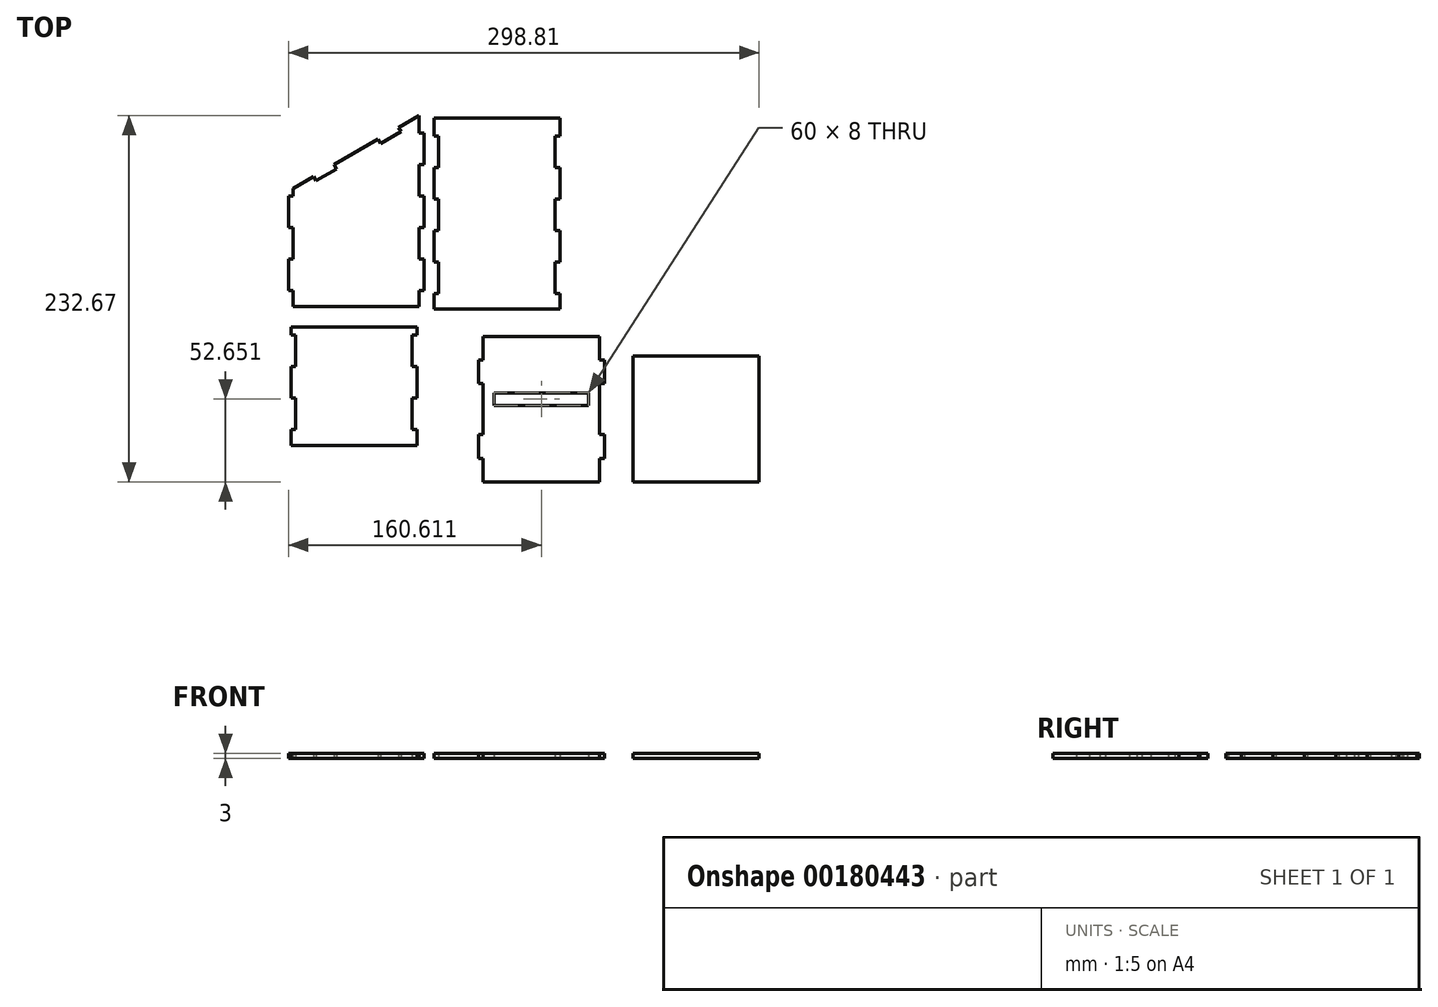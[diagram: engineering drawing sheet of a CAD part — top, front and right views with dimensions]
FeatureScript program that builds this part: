
annotation { "Feature Type Name" : "Feature", "Feature Type Description" : "" }
export const myFeature = defineFeature(function(context is Context, id is Id, definition is map)
    precondition{}
    {
        {
            var Q0;
            Q0=qCreatedBy(makeId("Top.planeOp"),FACE);
            var sketch = newSketch(context, id + "F0", { "sketchPlane" : qUnion([Q0])});
            skLineSegment(sketch, "E0.bottom", {"start": v(175, 135) * mm, "end": v(-175, 135) * mm, "construction": true});
            skLineSegment(sketch, "E0.top", {"start": v(175, -135) * mm, "end": v(-175, -135) * mm, "construction": true});
            skLineSegment(sketch, "E0.left", {"start": v(175, 135) * mm, "end": v(175, -135) * mm, "construction": true});
            skLineSegment(sketch, "E0.right", {"start": v(-175, 135) * mm, "end": v(-175, -135) * mm, "construction": true});
            skPoint(sketch, "E0.middle", {"position": v(0, 0) * mm});
            skLineSegment(sketch, "E1.bottom", {"start": v(-144.86, 75.27) * mm, "end": v(-131.87, 82.77) * mm});
            skLineSegment(sketch, "E1.top", {"start": v(-144.86, 0.27) * mm, "end": v(-64.86, 0.27) * mm});
            skLineSegment(sketch, "E1.left", {"start": v(-144.86, 75.27) * mm, "end": v(-144.86, 70.27) * mm});
            skLineSegment(sketch, "E1.right", {"start": v(-64.86, 121.46) * mm, "end": v(-64.86, 110.27) * mm});
            skLineSegment(sketch, "E2.bottom", {"start": v(-55.51, 119.78) * mm, "end": v(24.49, 119.78) * mm});
            skLineSegment(sketch, "E2.top", {"start": v(-55.51, -1.41) * mm, "end": v(24.49, -1.41) * mm});
            skLineSegment(sketch, "E2.left", {"start": v(-55.51, 119.78) * mm, "end": v(-55.51, 108.59) * mm});
            skLineSegment(sketch, "E2.right", {"start": v(24.49, 119.78) * mm, "end": v(24.49, 108.59) * mm});
            skLineSegment(sketch, "E3.bottom", {"start": v(52.66, 73.13) * mm, "end": v(132.66, 119.32) * mm});
            skLineSegment(sketch, "E3.top", {"start": v(52.66, -1.87) * mm, "end": v(132.66, -1.87) * mm});
            skLineSegment(sketch, "E3.left", {"start": v(52.66, 73.13) * mm, "end": v(52.66, -1.87) * mm});
            skLineSegment(sketch, "E3.right", {"start": v(132.66, 119.32) * mm, "end": v(132.66, -1.87) * mm});
            skLineSegment(sketch, "E4.bottom", {"start": v(-146.25, -12.92) * mm, "end": v(-66.25, -12.92) * mm});
            skLineSegment(sketch, "E4.top", {"start": v(-146.25, -87.92) * mm, "end": v(-66.25, -87.92) * mm});
            skLineSegment(sketch, "E4.left", {"start": v(-146.25, -12.92) * mm, "end": v(-146.25, -17.92) * mm});
            skLineSegment(sketch, "E4.right", {"start": v(-66.25, -12.92) * mm, "end": v(-66.25, -17.92) * mm});
            skLineSegment(sketch, "E5.bottom", {"start": v(-24.25, -18.83) * mm, "end": v(49.75, -18.83) * mm});
            skLineSegment(sketch, "E5.top", {"start": v(-24.25, -111.21) * mm, "end": v(49.75, -111.21) * mm});
            skLineSegment(sketch, "E5.left", {"start": v(-24.25, -18.83) * mm, "end": v(-24.25, -33.83) * mm});
            skLineSegment(sketch, "E5.right", {"start": v(49.75, -18.83) * mm, "end": v(49.75, -33.83) * mm});
            skLineSegment(sketch, "E6.bottom", {"start": v(-17.25, -54.56) * mm, "end": v(42.75, -54.56) * mm});
            skLineSegment(sketch, "E6.top", {"start": v(-17.25, -62.56) * mm, "end": v(42.75, -62.56) * mm});
            skLineSegment(sketch, "E6.left", {"start": v(-17.25, -54.56) * mm, "end": v(-17.25, -62.56) * mm});
            skLineSegment(sketch, "E6.right", {"start": v(42.75, -54.56) * mm, "end": v(42.75, -62.56) * mm});
            skLineSegment(sketch, "E7", {"start": v(12.75, -18.83) * mm, "end": v(12.75, -54.56) * mm, "construction": true});
            skLineSegment(sketch, "E8", {"start": v(-64.86, 70.27) * mm, "end": v(-61.86, 70.27) * mm});
            skLineSegment(sketch, "E9", {"start": v(-61.86, 70.27) * mm, "end": v(-61.86, 50.27) * mm});
            skLineSegment(sketch, "E10", {"start": v(-61.86, 50.27) * mm, "end": v(-64.86, 50.27) * mm});
            skLineSegment(sketch, "E11", {"start": v(-55.51, 68.59) * mm, "end": v(-52.51, 68.59) * mm});
            skLineSegment(sketch, "E12", {"start": v(-52.51, 68.59) * mm, "end": v(-52.51, 48.59) * mm});
            skLineSegment(sketch, "E13", {"start": v(-52.51, 48.59) * mm, "end": v(-55.51, 48.59) * mm});
            skLineSegment(sketch, "E14", {"start": v(-64.86, 30.27) * mm, "end": v(-61.86, 30.27) * mm});
            skLineSegment(sketch, "E15", {"start": v(-61.86, 30.27) * mm, "end": v(-61.86, 10.27) * mm});
            skLineSegment(sketch, "E16", {"start": v(-61.86, 10.27) * mm, "end": v(-64.86, 10.27) * mm});
            skLineSegment(sketch, "E17", {"start": v(-55.51, 28.59) * mm, "end": v(-52.51, 28.59) * mm});
            skLineSegment(sketch, "E18", {"start": v(-52.51, 28.59) * mm, "end": v(-52.51, 8.59) * mm});
            skLineSegment(sketch, "E19", {"start": v(-52.51, 8.59) * mm, "end": v(-55.51, 8.59) * mm});
            skLineSegment(sketch, "E20.trimOffspring", {"start": v(-64.86, 50.27) * mm, "end": v(-64.86, 30.27) * mm});
            skLineSegment(sketch, "E21.trimOffspring", {"start": v(-64.86, 10.27) * mm, "end": v(-64.86, 0.27) * mm});
            skLineSegment(sketch, "E22.trimOffspring", {"start": v(-55.51, 8.59) * mm, "end": v(-55.51, -1.41) * mm});
            skLineSegment(sketch, "E23.trimOffspring", {"start": v(-55.51, 48.59) * mm, "end": v(-55.51, 28.59) * mm});
            skLineSegment(sketch, "E24", {"start": v(-64.86, 90.27) * mm, "end": v(-61.86, 90.27) * mm});
            skLineSegment(sketch, "E25", {"start": v(-61.86, 90.27) * mm, "end": v(-61.86, 110.27) * mm});
            skLineSegment(sketch, "E26", {"start": v(-61.86, 110.27) * mm, "end": v(-64.86, 110.27) * mm});
            skLineSegment(sketch, "E27.trimOffspring", {"start": v(-64.86, 90.27) * mm, "end": v(-64.86, 70.27) * mm});
            skLineSegment(sketch, "E28", {"start": v(-55.51, 88.59) * mm, "end": v(-52.51, 88.59) * mm});
            skLineSegment(sketch, "E29", {"start": v(-52.51, 88.59) * mm, "end": v(-52.51, 108.59) * mm});
            skLineSegment(sketch, "E30", {"start": v(-52.51, 108.59) * mm, "end": v(-55.51, 108.59) * mm});
            skLineSegment(sketch, "E31.trimOffspring", {"start": v(-55.51, 88.59) * mm, "end": v(-55.51, 68.59) * mm});
            skLineSegment(sketch, "E32", {"start": v(24.49, 108.59) * mm, "end": v(21.49, 108.59) * mm});
            skLineSegment(sketch, "E33", {"start": v(21.49, 108.59) * mm, "end": v(21.49, 88.59) * mm});
            skLineSegment(sketch, "E34", {"start": v(21.49, 88.59) * mm, "end": v(24.49, 88.59) * mm});
            skLineSegment(sketch, "E35", {"start": v(24.49, 68.59) * mm, "end": v(21.49, 68.59) * mm});
            skLineSegment(sketch, "E36", {"start": v(21.49, 68.59) * mm, "end": v(21.49, 48.59) * mm});
            skLineSegment(sketch, "E37", {"start": v(21.49, 48.59) * mm, "end": v(24.49, 48.59) * mm});
            skLineSegment(sketch, "E38", {"start": v(24.49, 28.59) * mm, "end": v(21.49, 28.59) * mm});
            skLineSegment(sketch, "E39", {"start": v(21.49, 28.59) * mm, "end": v(21.49, 8.59) * mm});
            skLineSegment(sketch, "E40", {"start": v(21.49, 8.59) * mm, "end": v(24.49, 8.59) * mm});
            skLineSegment(sketch, "E41.trimOffspring", {"start": v(24.49, 88.59) * mm, "end": v(24.49, 68.59) * mm});
            skLineSegment(sketch, "E42.trimOffspring", {"start": v(24.49, 48.59) * mm, "end": v(24.49, 28.59) * mm});
            skLineSegment(sketch, "E43.trimOffspring", {"start": v(24.49, 8.59) * mm, "end": v(24.49, -1.41) * mm});
            skLineSegment(sketch, "E44", {"start": v(-144.86, 70.27) * mm, "end": v(-147.86, 70.27) * mm});
            skLineSegment(sketch, "E45", {"start": v(-147.86, 70.27) * mm, "end": v(-147.86, 50.27) * mm});
            skLineSegment(sketch, "E46", {"start": v(-147.86, 50.27) * mm, "end": v(-144.86, 50.27) * mm});
            skLineSegment(sketch, "E47", {"start": v(-144.86, 30.27) * mm, "end": v(-147.86, 30.27) * mm});
            skLineSegment(sketch, "E48", {"start": v(-147.86, 30.27) * mm, "end": v(-147.86, 10.27) * mm});
            skLineSegment(sketch, "E49", {"start": v(-147.86, 10.27) * mm, "end": v(-144.86, 10.27) * mm});
            skLineSegment(sketch, "E50.trimOffspring", {"start": v(-144.86, 50.27) * mm, "end": v(-144.86, 30.27) * mm});
            skLineSegment(sketch, "E51.trimOffspring", {"start": v(-144.86, 10.27) * mm, "end": v(-144.86, 0.27) * mm});
            skLineSegment(sketch, "E52", {"start": v(-66.25, -17.92) * mm, "end": v(-69.25, -17.92) * mm});
            skLineSegment(sketch, "E53", {"start": v(-69.25, -17.92) * mm, "end": v(-69.25, -37.92) * mm});
            skLineSegment(sketch, "E54", {"start": v(-69.25, -37.92) * mm, "end": v(-66.25, -37.92) * mm});
            skLineSegment(sketch, "E55", {"start": v(-66.25, -57.92) * mm, "end": v(-69.25, -57.92) * mm});
            skLineSegment(sketch, "E56", {"start": v(-69.25, -57.92) * mm, "end": v(-69.25, -77.92) * mm});
            skLineSegment(sketch, "E57", {"start": v(-69.25, -77.92) * mm, "end": v(-66.25, -77.92) * mm});
            skLineSegment(sketch, "E58", {"start": v(-146.25, -17.92) * mm, "end": v(-143.25, -17.92) * mm});
            skLineSegment(sketch, "E59", {"start": v(-143.25, -17.92) * mm, "end": v(-143.25, -37.92) * mm});
            skLineSegment(sketch, "E60", {"start": v(-143.25, -37.92) * mm, "end": v(-146.25, -37.92) * mm});
            skLineSegment(sketch, "E61", {"start": v(-146.25, -57.92) * mm, "end": v(-143.25, -57.92) * mm});
            skLineSegment(sketch, "E62", {"start": v(-143.25, -57.92) * mm, "end": v(-143.25, -77.92) * mm});
            skLineSegment(sketch, "E63", {"start": v(-143.25, -77.92) * mm, "end": v(-146.25, -77.92) * mm});
            skLineSegment(sketch, "E64.trimOffspring", {"start": v(-146.25, -37.92) * mm, "end": v(-146.25, -57.92) * mm});
            skLineSegment(sketch, "E65.trimOffspring", {"start": v(-146.25, -77.92) * mm, "end": v(-146.25, -87.92) * mm});
            skLineSegment(sketch, "E66.trimOffspring", {"start": v(-66.25, -37.92) * mm, "end": v(-66.25, -57.92) * mm});
            skLineSegment(sketch, "E67.trimOffspring", {"start": v(-66.25, -77.92) * mm, "end": v(-66.25, -87.92) * mm});
            skLineSegment(sketch, "E68", {"start": v(-131.87, 82.77) * mm, "end": v(-130.37, 80.17) * mm});
            skLineSegment(sketch, "E69", {"start": v(-130.37, 80.17) * mm, "end": v(-117.38, 87.67) * mm});
            skLineSegment(sketch, "E70", {"start": v(-117.38, 87.67) * mm, "end": v(-118.88, 90.27) * mm});
            skLineSegment(sketch, "E71", {"start": v(-90.84, 106.46) * mm, "end": v(-89.34, 103.86) * mm});
            skLineSegment(sketch, "E72", {"start": v(-89.34, 103.86) * mm, "end": v(-76.35, 111.36) * mm});
            skLineSegment(sketch, "E73", {"start": v(-76.35, 111.36) * mm, "end": v(-77.85, 113.96) * mm});
            skLineSegment(sketch, "E74.trimOffspring", {"start": v(-77.85, 113.96) * mm, "end": v(-64.86, 121.46) * mm});
            skLineSegment(sketch, "E75.trimOffspring", {"start": v(-118.88, 90.27) * mm, "end": v(-90.84, 106.46) * mm});
            skLineSegment(sketch, "E76", {"start": v(-24.25, -33.83) * mm, "end": v(-27.25, -33.83) * mm});
            skLineSegment(sketch, "E77", {"start": v(-27.25, -33.83) * mm, "end": v(-27.25, -48.83) * mm});
            skLineSegment(sketch, "E78", {"start": v(-27.25, -48.83) * mm, "end": v(-24.25, -48.83) * mm});
            skLineSegment(sketch, "E79", {"start": v(-24.25, -96.21) * mm, "end": v(-27.25, -96.21) * mm});
            skLineSegment(sketch, "E80", {"start": v(-27.25, -96.21) * mm, "end": v(-27.25, -81.21) * mm});
            skLineSegment(sketch, "E81", {"start": v(-27.25, -81.21) * mm, "end": v(-24.25, -81.21) * mm});
            skLineSegment(sketch, "E82", {"start": v(49.75, -33.83) * mm, "end": v(52.75, -33.83) * mm});
            skLineSegment(sketch, "E83", {"start": v(52.75, -33.83) * mm, "end": v(52.75, -48.83) * mm});
            skLineSegment(sketch, "E84", {"start": v(52.75, -48.83) * mm, "end": v(49.75, -48.83) * mm});
            skLineSegment(sketch, "E85", {"start": v(49.75, -96.21) * mm, "end": v(52.75, -96.21) * mm});
            skLineSegment(sketch, "E86", {"start": v(52.75, -96.21) * mm, "end": v(52.75, -81.21) * mm});
            skLineSegment(sketch, "E87", {"start": v(52.75, -81.21) * mm, "end": v(49.75, -81.21) * mm});
            skLineSegment(sketch, "E88.trimOffspring", {"start": v(-24.25, -48.83) * mm, "end": v(-24.25, -81.21) * mm});
            skLineSegment(sketch, "E89.trimOffspring", {"start": v(-24.25, -96.21) * mm, "end": v(-24.25, -111.21) * mm});
            skLineSegment(sketch, "E90.trimOffspring", {"start": v(49.75, -48.83) * mm, "end": v(49.75, -81.21) * mm});
            skLineSegment(sketch, "E91.trimOffspring", {"start": v(49.75, -96.21) * mm, "end": v(49.75, -111.21) * mm});
            skLineSegment(sketch, "E92", {"start": v(-27.25, -33.83) * mm, "end": v(52.75, -33.83) * mm, "construction": true});
            skLineSegment(sketch, "E93.bottom", {"start": v(70.95, -31.2) * mm, "end": v(150.95, -31.2) * mm});
            skLineSegment(sketch, "E93.top", {"start": v(70.95, -111.2) * mm, "end": v(150.95, -111.2) * mm});
            skLineSegment(sketch, "E93.left", {"start": v(70.95, -31.2) * mm, "end": v(70.95, -111.2) * mm});
            skLineSegment(sketch, "E93.right", {"start": v(150.95, -31.2) * mm, "end": v(150.95, -111.2) * mm});
            skSolve(sketch);
        }
        {
            var Q0;
            Q0=makeQuery(id+"F0.imprint","IMPRINT",FACE,{"disambiguationData":[TD([[makeQuery(id+"F0.imprint","IMPRINT",EDGE,{"derivedFrom":sQuery(id+"F0.wireOp",EDGE,"E1.bottom")}),-1.0]])]});
            var Q1;
            Q1=makeQuery(id+"F0.imprint","IMPRINT",FACE,{"disambiguationData":[TD([[makeQuery(id+"F0.imprint","IMPRINT",EDGE,{"derivedFrom":sQuery(id+"F0.wireOp",EDGE,"E2.bottom")}),-1.0]])]});
            var Q2;
            Q2=makeQuery(id+"F0.imprint","IMPRINT",FACE,{"disambiguationData":[TD([[makeQuery(id+"F0.imprint","IMPRINT",EDGE,{"derivedFrom":sQuery(id+"F0.wireOp",EDGE,"E4.bottom")}),-1.0]])]});
            var Q3;
            Q3=makeQuery(id+"F0.imprint","IMPRINT",FACE,{"disambiguationData":[TD([[makeQuery(id+"F0.imprint","IMPRINT",EDGE,{"derivedFrom":sQuery(id+"F0.wireOp",EDGE,"E5.bottom")}),-1.0]])]});
            var Q4;
            Q4=makeQuery(id+"F0.imprint","IMPRINT",FACE,{"disambiguationData":[TD([[makeQuery(id+"F0.imprint","IMPRINT",EDGE,{"derivedFrom":sQuery(id+"F0.wireOp",EDGE,"E93.bottom")}),-1.0]])]});
            extrude(context, id + "F1", {"entities" : qUnion([Q0, Q1, Q2, Q3, Q4]), "depth" : 3 * mm});
        }
    });
